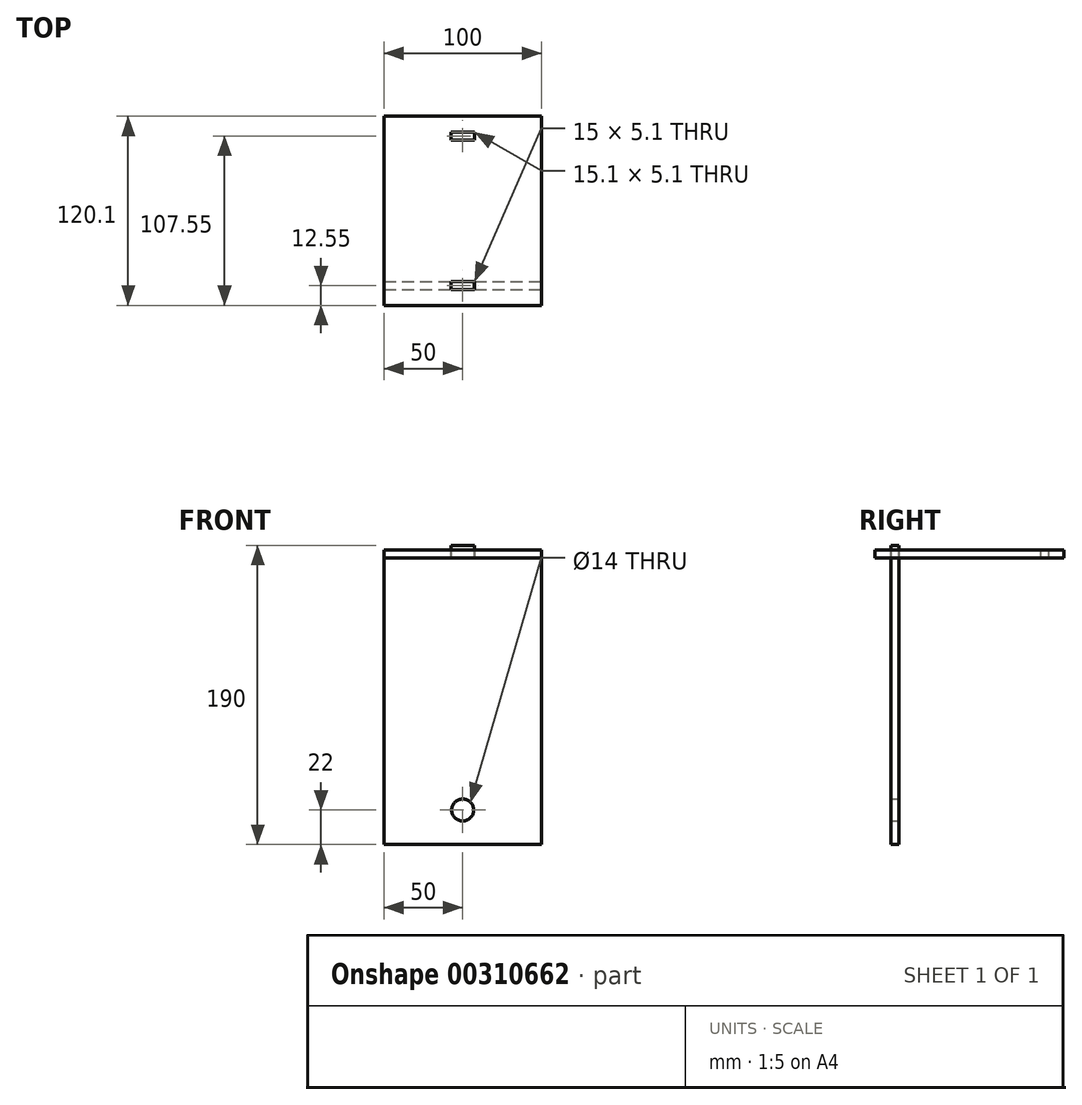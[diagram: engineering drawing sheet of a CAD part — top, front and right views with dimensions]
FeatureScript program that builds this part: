
annotation { "Feature Type Name" : "Feature", "Feature Type Description" : "" }
export const myFeature = defineFeature(function(context is Context, id is Id, definition is map)
    precondition{}
    {
        {
            var Q0;
            Q0=qCreatedBy(makeId("Front.planeOp"),FACE);
            var sketch = newSketch(context, id + "F0", { "sketchPlane" : qUnion([Q0])});
            skLineSegment(sketch, "E0.bottom", {"start": v(0, 0) * mm, "end": v(100, 0) * mm});
            skLineSegment(sketch, "E0.top", {"start": v(0, 182) * mm, "end": v(100, 182) * mm});
            skLineSegment(sketch, "E0.left", {"start": v(0, 0) * mm, "end": v(0, 182) * mm});
            skLineSegment(sketch, "E0.right", {"start": v(100, 0) * mm, "end": v(100, 182) * mm});
            skCircle(sketch, "E1", {"center": v(50, 22) * mm, "radius": 7 * mm});
            skPoint(sketch, "E2", {"position": v(50, 182) * mm});
            skLineSegment(sketch, "E3.bottom", {"start": v(42.5, 182) * mm, "end": v(57.5, 182) * mm});
            skLineSegment(sketch, "E3.top", {"start": v(42.5, 190) * mm, "end": v(57.5, 190) * mm});
            skLineSegment(sketch, "E3.left", {"start": v(42.5, 182) * mm, "end": v(42.5, 190) * mm});
            skLineSegment(sketch, "E3.right", {"start": v(57.5, 182) * mm, "end": v(57.5, 190) * mm});
            skPoint(sketch, "E4", {"position": v(50, 190) * mm});
            skSolve(sketch);
        }
        {
            var Q0;
            Q0 = qSketchRegion(id + "F0", true);
            extrude(context, id + "F1", {"entities" : qUnion([Q0]), "depth" : 5 * mm});
        }
        {
            var Q0;
            {var subQ0=sQuery(id+"F0.wireOp",EDGE,"E0.top");Q0=makeQuery(id+"F1.opExtrude","SWEPT_FACE",FACE,{"disambiguationData":[OSD([subQ0]),TDD([makeQuery(id+"F0.imprint","IMPRINT",EDGE,{"disambiguationData":[TD([[makeQuery(id+"F0.imprint","INTERSECT",VERTEX,{"derivedFrom":[subQ0,sQuery(id+"F0.wireOp",EDGE,"E0.left")]}),-1.0]])],"derivedFrom":subQ0})])]});}
            var sketch = newSketch(context, id + "F2", { "sketchPlane" : qUnion([Q0])});
            skLineSegment(sketch, "E5.bottom", {"start": v(0, -15.05) * mm, "end": v(100, -15.05) * mm});
            skLineSegment(sketch, "E5.top", {"start": v(0, 105.05) * mm, "end": v(100, 105.05) * mm});
            skLineSegment(sketch, "E5.left", {"start": v(0, -15.05) * mm, "end": v(0, 105.05) * mm});
            skLineSegment(sketch, "E5.right", {"start": v(100, -15.05) * mm, "end": v(100, 105.05) * mm});
            skLineSegment(sketch, "E6.bottom", {"start": v(42.45, 95.05) * mm, "end": v(57.55, 95.05) * mm});
            skLineSegment(sketch, "E6.top", {"start": v(42.45, 89.95) * mm, "end": v(57.55, 89.95) * mm});
            skLineSegment(sketch, "E6.left", {"start": v(42.45, 95.05) * mm, "end": v(42.45, 89.95) * mm});
            skLineSegment(sketch, "E6.right", {"start": v(57.55, 95.05) * mm, "end": v(57.55, 89.95) * mm});
            skLineSegment(sketch, "E7.bottom", {"start": v(42.5, 0.05) * mm, "end": v(57.5, 0.05) * mm});
            skLineSegment(sketch, "E7.top", {"start": v(42.5, -5.05) * mm, "end": v(57.5, -5.05) * mm});
            skLineSegment(sketch, "E7.left", {"start": v(42.5, 0.05) * mm, "end": v(42.5, -5.05) * mm});
            skLineSegment(sketch, "E7.right", {"start": v(57.5, 0.05) * mm, "end": v(57.5, -5.05) * mm});
            skPoint(sketch, "E8", {"position": v(50, 105.05) * mm});
            skPoint(sketch, "E9", {"position": v(50, 95.05) * mm});
            skPoint(sketch, "E10", {"position": v(50, -5.05) * mm});
            skSolve(sketch);
        }
        {
            var Q0;
            Q0 = qSketchRegion(id + "F2", true);
            extrude(context, id + "F3", {"entities" : qUnion([Q0]), "depth" : 5 * mm});
        }
    });
